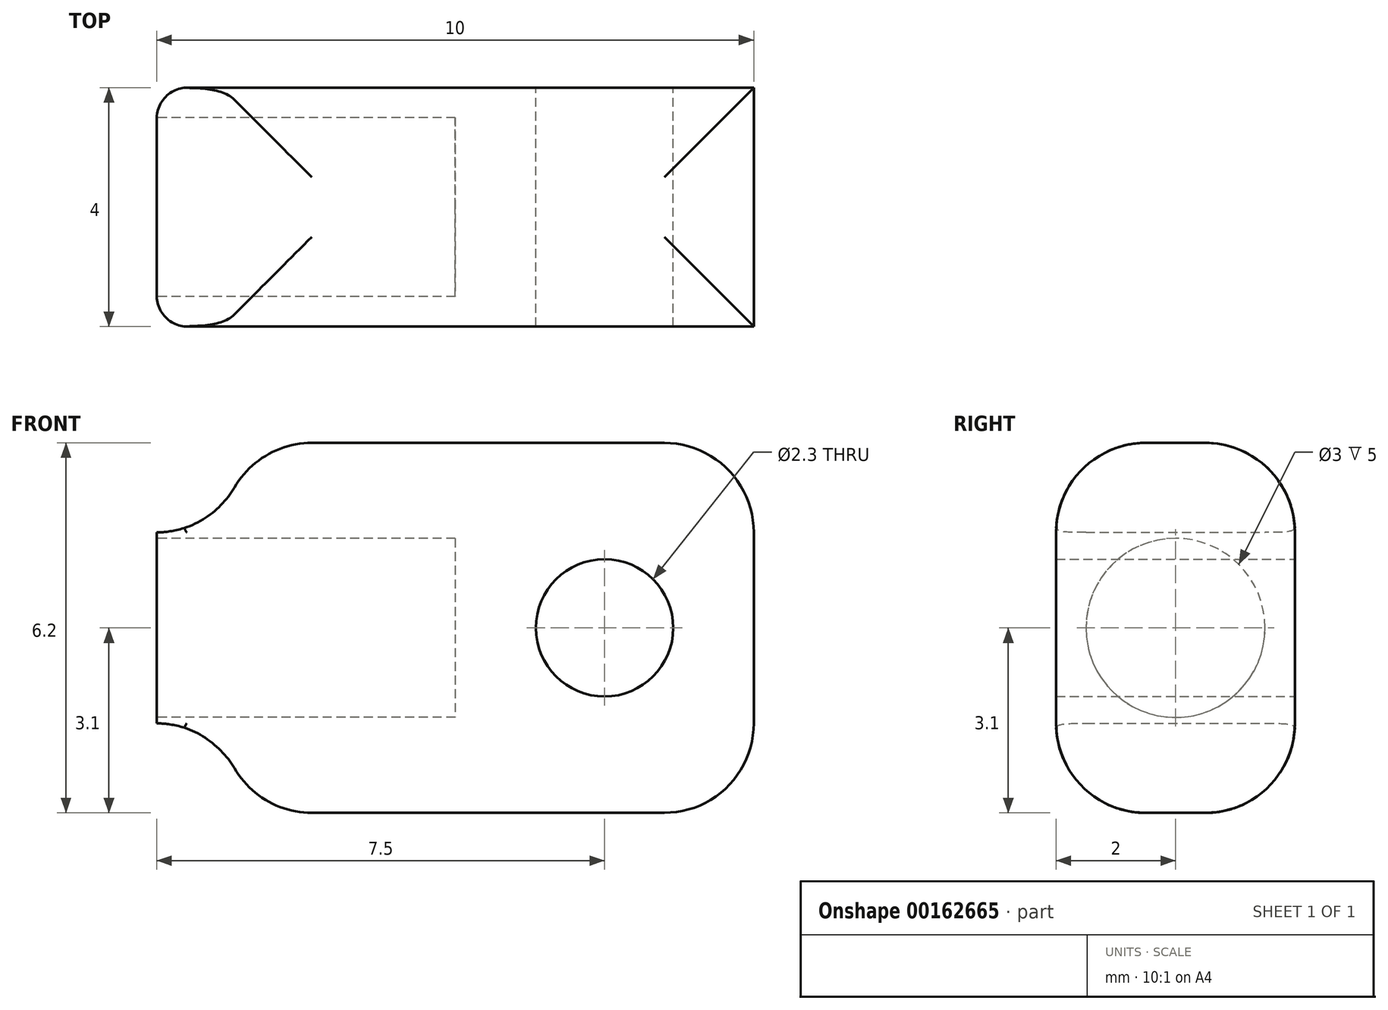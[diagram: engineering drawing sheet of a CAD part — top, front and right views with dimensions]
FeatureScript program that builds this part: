
annotation { "Feature Type Name" : "Feature", "Feature Type Description" : "" }
export const myFeature = defineFeature(function(context is Context, id is Id, definition is map)
    precondition{}
    {
        {
            var Q0;
            Q0=qCreatedBy(makeId("Front.planeOp"),FACE);
            var sketch = newSketch(context, id + "F0", { "sketchPlane" : qUnion([Q0])});
            skLineSegment(sketch, "E0.bottom", {"start": v(-3.5, 3.1) * mm, "end": v(5, 3.1) * mm});
            skLineSegment(sketch, "E0.top", {"start": v(-3.5, -3.1) * mm, "end": v(5, -3.1) * mm});
            skLineSegment(sketch, "E0.left", {"start": v(-5, 1.6) * mm, "end": v(-5, -1.6) * mm});
            skLineSegment(sketch, "E0.right", {"start": v(5, 3.1) * mm, "end": v(5, -3.1) * mm});
            skPoint(sketch, "E0.middle", {"position": v(0, 0) * mm});
            skArc(sketch, "E1", {"start": v(-5, 1.6) * mm, "mid": v(-3.94, 2.04) * mm, "end": v(-3.5, 3.1) * mm});
            skArc(sketch, "E2.MirrorCS", {"start": v(-5, -1.6) * mm, "mid": v(-3.94, -2.04) * mm, "end": v(-3.5, -3.1) * mm});
            skCircle(sketch, "E3", {"center": v(2.5, 0) * mm, "radius": 1.15 * mm});
            skSolve(sketch);
        }
        {
            var Q0;
            Q0 = qSketchRegion(id + "F0", true);
            extrude(context, id + "F1", {"entities" : qUnion([Q0]), "depth" : 4 * mm, "offsetDistance" : 25 * mm, "symmetric" : true});
        }
        {
            var Q0;
            Q0=makeQuery(id+"F1.opExtrude","CAP_EDGE",EDGE,{"disambiguationData":[OSD([sQuery(id+"F0.wireOp",EDGE,"E0.bottom")])],"isStart":false});
            var Q1;
            Q1=makeQuery(id+"F1.opExtrude","SWEPT_FACE",FACE,{"disambiguationData":[OSD([sQuery(id+"F0.wireOp",EDGE,"E0.bottom")])]});
            var Q2;
            Q2=makeQuery(id+"F1.opExtrude","SWEPT_FACE",FACE,{"disambiguationData":[OSD([sQuery(id+"F0.wireOp",EDGE,"E0.top")])]});
            fillet(context, id + "F2", {"entities" : qUnion([Q0, Q1, Q2]), "radius" : 1.5 * mm, "tangentPropagation" : true, "allowEdgeOverflow" : false});
        }
        {
            var Q0;
            Q0=makeQuery(id+"F1.opExtrude","SWEPT_FACE",FACE,{"disambiguationData":[OSD([sQuery(id+"F0.wireOp",EDGE,"E0.left")])]});
            var sketch = newSketch(context, id + "F3", { "sketchPlane" : qUnion([Q0])});
            skCircle(sketch, "E4", {"center": v(0, 0) * mm, "radius": 1.5 * mm});
            skSolve(sketch);
        }
        {
            var Q0;
            Q0=makeQuery(id+"F1.opExtrude","CAP_EDGE",EDGE,{"disambiguationData":[OSD([sQuery(id+"F0.wireOp",EDGE,"E0.left")])],"isStart":false});
            var Q1;
            Q1=makeQuery(id+"F1.opExtrude","CAP_EDGE",EDGE,{"disambiguationData":[OSD([sQuery(id+"F0.wireOp",EDGE,"E0.left")])],"isStart":true});
            fillet(context, id + "F4", {"entities" : qUnion([Q0, Q1]), "radius" : .5 * mm, "tangentPropagation" : true, "allowEdgeOverflow" : false});
        }
        {
            var Q0;
            Q0=makeQuery(id+"F3.imprint","IMPRINT",FACE,{"disambiguationData":[TD([[makeQuery(id+"F3.imprint","IMPRINT",EDGE,{"derivedFrom":sQuery(id+"F3.wireOp",EDGE,"E4")}),1.0]])]});
            extrude(context, id + "F5", {"entities" : qUnion([Q0]), "operationType" : NewBodyOperationType.REMOVE, "oppositeDirection" : true, "depth" : 5 * mm, "offsetDistance" : 25 * mm});
        }
    });
